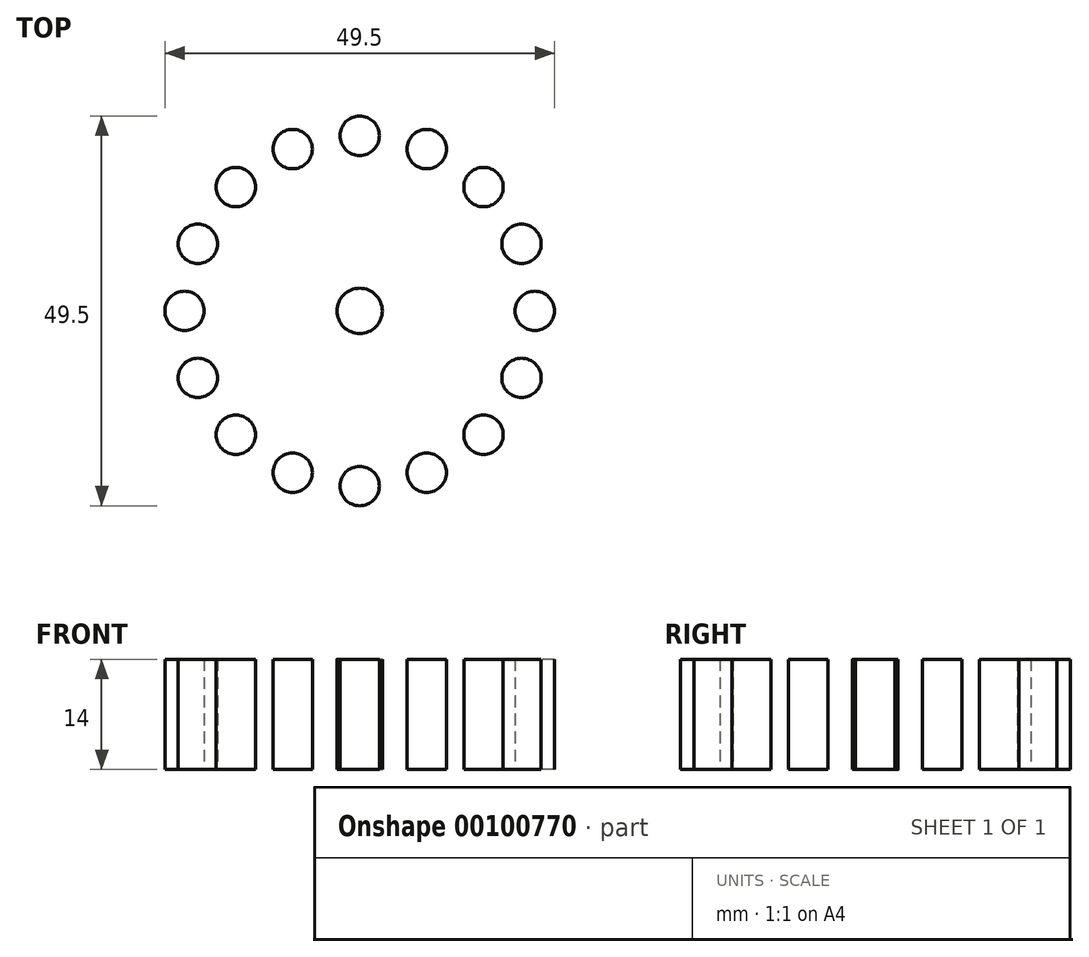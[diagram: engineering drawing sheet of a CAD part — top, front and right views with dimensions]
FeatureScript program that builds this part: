
annotation { "Feature Type Name" : "Feature", "Feature Type Description" : "" }
export const myFeature = defineFeature(function(context is Context, id is Id, definition is map)
    precondition{}
    {
        {
            var Q0;
            Q0=qCreatedBy(makeId("Top.planeOp"),FACE);
            var sketch = newSketch(context, id + "F0", { "sketchPlane" : qUnion([Q0])});
            skCircle(sketch, "E0", {"center": v(0, 0) * mm, "radius": 20 * mm, "construction": true});
            skCircle(sketch, "E1", {"center": v(0, 0) * mm, "radius": 24.5 * mm, "construction": true});
            skLineSegment(sketch, "E2", {"start": v(0, 20) * mm, "end": v(0, 24.5) * mm, "construction": true});
            skCircle(sketch, "E3", {"center": v(0, 22.25) * mm, "radius": 2.5 * mm});
            skCircle(sketch, "E4.1.0", {"center": v(-8.51, 20.56) * mm, "radius": 2.5 * mm});
            skCircle(sketch, "E4.2.0", {"center": v(-15.73, 15.73) * mm, "radius": 2.5 * mm});
            skCircle(sketch, "E4.3.0", {"center": v(-20.56, 8.51) * mm, "radius": 2.5 * mm});
            skCircle(sketch, "E4.4.0", {"center": v(-22.25, 0) * mm, "radius": 2.5 * mm});
            skCircle(sketch, "E4.5.0", {"center": v(-20.56, -8.51) * mm, "radius": 2.5 * mm});
            skCircle(sketch, "E4.6.0", {"center": v(-15.73, -15.73) * mm, "radius": 2.5 * mm});
            skCircle(sketch, "E4.7.0", {"center": v(-8.51, -20.56) * mm, "radius": 2.5 * mm});
            skCircle(sketch, "E4.8.0", {"center": v(0, -22.25) * mm, "radius": 2.5 * mm});
            skCircle(sketch, "E4.9.0", {"center": v(8.51, -20.56) * mm, "radius": 2.5 * mm});
            skCircle(sketch, "E4.10.0", {"center": v(15.73, -15.73) * mm, "radius": 2.5 * mm});
            skCircle(sketch, "E4.11.0", {"center": v(20.56, -8.51) * mm, "radius": 2.5 * mm});
            skCircle(sketch, "E4.12.0", {"center": v(22.25, 0) * mm, "radius": 2.5 * mm});
            skCircle(sketch, "E4.13.0", {"center": v(20.56, 8.51) * mm, "radius": 2.5 * mm});
            skCircle(sketch, "E4.14.0", {"center": v(15.73, 15.73) * mm, "radius": 2.5 * mm});
            skCircle(sketch, "E4.15.0", {"center": v(8.51, 20.56) * mm, "radius": 2.5 * mm});
            skLineSegment(sketch, "E5", {"start": v(20.56, 8.51) * mm, "end": v(0, 0) * mm, "construction": true});
            skLineSegment(sketch, "E6", {"start": v(0, 0) * mm, "end": v(22.25, 0) * mm, "construction": true});
            skLineSegment(sketch, "E7", {"start": v(22.25, 0) * mm, "end": v(20.56, 8.51) * mm, "construction": true});
            skCircle(sketch, "E8", {"center": v(0, 0) * mm, "radius": 2.87 * mm});
            skSolve(sketch);
        }
        {
            var Q0;
            Q0=makeQuery(id+"F0.imprint","IMPRINT",FACE,{"disambiguationData":[TD([[makeQuery(id+"F0.imprint","IMPRINT",EDGE,{"derivedFrom":sQuery(id+"F0.wireOp",EDGE,"E4.15.0")}),1.0]])]});
            var Q1;
            Q1=makeQuery(id+"F0.imprint","IMPRINT",FACE,{"disambiguationData":[TD([[makeQuery(id+"F0.imprint","IMPRINT",EDGE,{"derivedFrom":sQuery(id+"F0.wireOp",EDGE,"E4.13.0")}),1.0]])]});
            var Q2;
            Q2=makeQuery(id+"F0.imprint","IMPRINT",FACE,{"disambiguationData":[TD([[makeQuery(id+"F0.imprint","IMPRINT",EDGE,{"derivedFrom":sQuery(id+"F0.wireOp",EDGE,"E4.14.0")}),1.0]])]});
            var Q3;
            Q3=makeQuery(id+"F0.imprint","IMPRINT",FACE,{"disambiguationData":[TD([[makeQuery(id+"F0.imprint","IMPRINT",EDGE,{"derivedFrom":sQuery(id+"F0.wireOp",EDGE,"E3")}),1.0]])]});
            var Q4;
            Q4=makeQuery(id+"F0.imprint","IMPRINT",FACE,{"disambiguationData":[TD([[makeQuery(id+"F0.imprint","IMPRINT",EDGE,{"derivedFrom":sQuery(id+"F0.wireOp",EDGE,"E4.1.0")}),1.0]])]});
            var Q5;
            Q5=makeQuery(id+"F0.imprint","IMPRINT",FACE,{"disambiguationData":[TD([[makeQuery(id+"F0.imprint","IMPRINT",EDGE,{"derivedFrom":sQuery(id+"F0.wireOp",EDGE,"E4.2.0")}),1.0]])]});
            var Q6;
            Q6=makeQuery(id+"F0.imprint","IMPRINT",FACE,{"disambiguationData":[TD([[makeQuery(id+"F0.imprint","IMPRINT",EDGE,{"derivedFrom":sQuery(id+"F0.wireOp",EDGE,"E4.3.0")}),1.0]])]});
            var Q7;
            Q7=makeQuery(id+"F0.imprint","IMPRINT",FACE,{"disambiguationData":[TD([[makeQuery(id+"F0.imprint","IMPRINT",EDGE,{"derivedFrom":sQuery(id+"F0.wireOp",EDGE,"E4.4.0")}),1.0]])]});
            var Q8;
            Q8=makeQuery(id+"F0.imprint","IMPRINT",FACE,{"disambiguationData":[TD([[makeQuery(id+"F0.imprint","IMPRINT",EDGE,{"derivedFrom":sQuery(id+"F0.wireOp",EDGE,"E4.5.0")}),1.0]])]});
            var Q9;
            Q9=makeQuery(id+"F0.imprint","IMPRINT",FACE,{"disambiguationData":[TD([[makeQuery(id+"F0.imprint","IMPRINT",EDGE,{"derivedFrom":sQuery(id+"F0.wireOp",EDGE,"E4.6.0")}),1.0]])]});
            var Q10;
            Q10=makeQuery(id+"F0.imprint","IMPRINT",FACE,{"disambiguationData":[TD([[makeQuery(id+"F0.imprint","IMPRINT",EDGE,{"derivedFrom":sQuery(id+"F0.wireOp",EDGE,"E4.7.0")}),1.0]])]});
            var Q11;
            Q11=makeQuery(id+"F0.imprint","IMPRINT",FACE,{"disambiguationData":[TD([[makeQuery(id+"F0.imprint","IMPRINT",EDGE,{"derivedFrom":sQuery(id+"F0.wireOp",EDGE,"E4.8.0")}),1.0]])]});
            var Q12;
            Q12=makeQuery(id+"F0.imprint","IMPRINT",FACE,{"disambiguationData":[TD([[makeQuery(id+"F0.imprint","IMPRINT",EDGE,{"derivedFrom":sQuery(id+"F0.wireOp",EDGE,"E4.9.0")}),1.0]])]});
            var Q13;
            Q13=makeQuery(id+"F0.imprint","IMPRINT",FACE,{"disambiguationData":[TD([[makeQuery(id+"F0.imprint","IMPRINT",EDGE,{"derivedFrom":sQuery(id+"F0.wireOp",EDGE,"E4.10.0")}),1.0]])]});
            var Q14;
            Q14=makeQuery(id+"F0.imprint","IMPRINT",FACE,{"disambiguationData":[TD([[makeQuery(id+"F0.imprint","IMPRINT",EDGE,{"derivedFrom":sQuery(id+"F0.wireOp",EDGE,"E4.11.0")}),1.0]])]});
            var Q15;
            Q15=makeQuery(id+"F0.imprint","IMPRINT",FACE,{"disambiguationData":[TD([[makeQuery(id+"F0.imprint","IMPRINT",EDGE,{"derivedFrom":sQuery(id+"F0.wireOp",EDGE,"E4.12.0")}),1.0]])]});
            var Q16;
            Q16=makeQuery(id+"F0.imprint","IMPRINT",FACE,{"disambiguationData":[TD([[makeQuery(id+"F0.imprint","IMPRINT",EDGE,{"derivedFrom":sQuery(id+"F0.wireOp",EDGE,"E8")}),1.0]])]});
            extrude(context, id + "F1", {"entities" : qUnion([Q0, Q1, Q2, Q3, Q4, Q5, Q6, Q7, Q8, Q9, Q10, Q11, Q12, Q13, Q14, Q15, Q16]), "depth" : 14 * mm});
        }
    });
